# Revit family: 2-5154-124 Epoch
name_source: partatom
category: Lighting Fixtures
revit_build: Autodesk Revit LT 2014 (Build: 20130308_1515(x64)
units: mm (PartAtom-declared; Revit-internal decimal feet)

## types (1)
- 2-5154-124 Epoch
    ADA Compliant = Yes
    Apparent Load = 18 VA
    Ballast Manufacturer = Fulham RHA-UNV-218-C
    Color Filter = 16777215
    Default Elevation = 4' - 0"
    Description = 15.75" Wall Sconce
    Diffuser = 1 - White Cotton Shade
    Dimming Lamp Color Temperature Shift = <None>
    Emit Shape Visible in Rendering = No
    Emit from Rectangle Length = 4' - 0"
    Emit from Rectangle Width = 2' - 0"
    Fixture Height = 1' - 3 3/4"
    Fixture Width = 0' - 5 1/8"
    Input Power = 18.3
    Input Voltage = 120
    Junction Box = 4" Octagonal
    Lamp = 1x18W quad 4-pin fluorescent G24q-2
    Lamp Manufacturer = Sylvania
    Manufacturer = Oxygen Lighting
    Metal Finish = 24 - Satin Nickel
    Model = 2-5154-124
    Photometric Web File = 2-5154-124.IES
    Power Factor = 0.99
    Shade Height = 0' - 8 1/4"
    Tilt Angle = 180.00°
    Type Comments = Lighting - Fluorescent
    URL = http://www.oxygenlighting.com

## geometry (parser evidence)
native form markers: Sweep x1
no freeform markers — native parametric forms only
